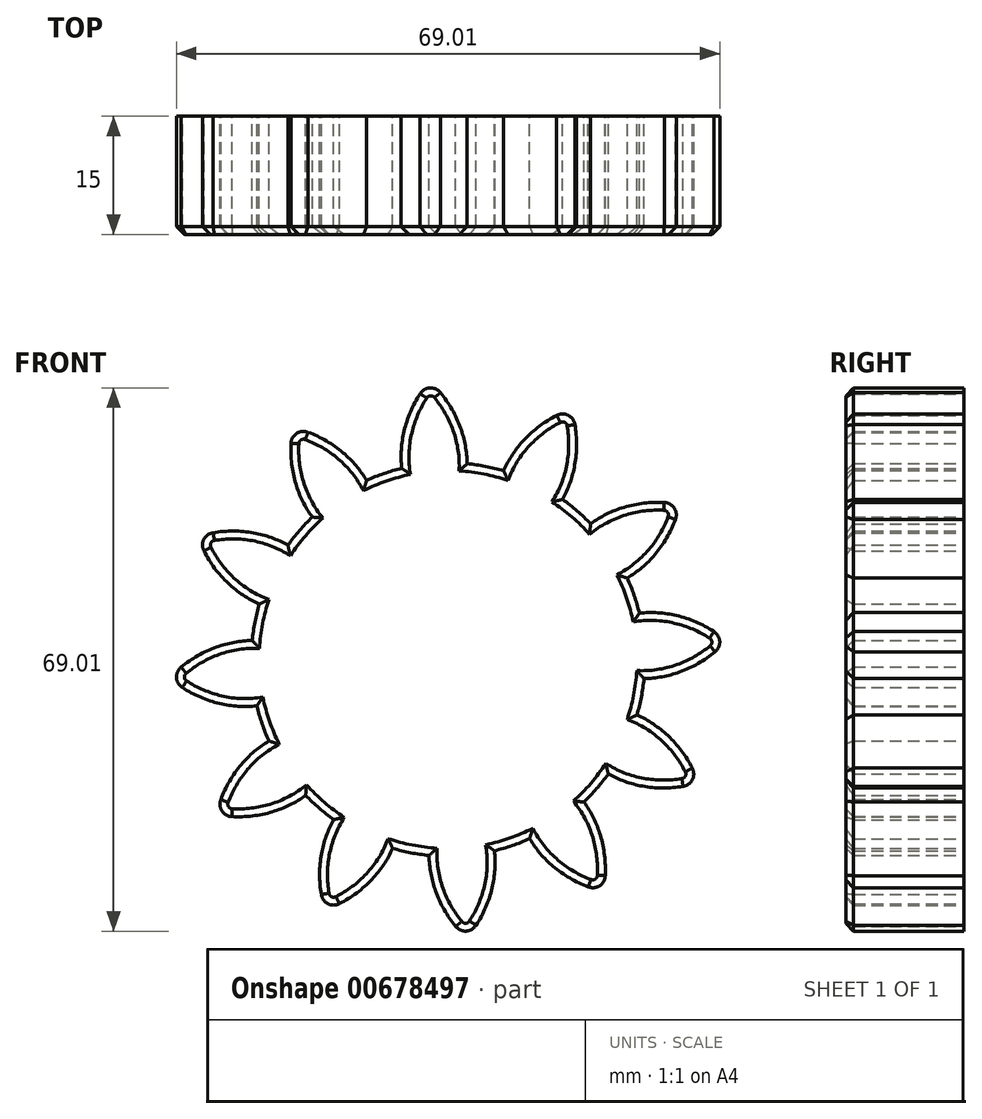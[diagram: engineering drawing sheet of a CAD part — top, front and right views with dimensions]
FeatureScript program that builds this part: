
annotation { "Feature Type Name" : "Feature", "Feature Type Description" : "" }
export const myFeature = defineFeature(function(context is Context, id is Id, definition is map)
    precondition{}
    {
        {
            var Q0;
            Q0=qCreatedBy(makeId("Front.planeOp"),FACE);
            var sketch = newSketch(context, id + "F0", { "sketchPlane" : qUnion([Q0])});
            skLineSegment(sketch, "E0", {"start": v(0, 27.14) * mm, "end": v(-50.23, 27.14) * mm, "construction": true});
            skArc(sketch, "E1", {"start": v(1.46, 32.31) * mm, "mid": v(0.38, 34.66) * mm, "end": v(-1.1, 36.8) * mm});
            skArc(sketch, "E2", {"start": v(2.3, 27.66) * mm, "mid": v(2.08, 30.02) * mm, "end": v(1.46, 32.31) * mm});
            skArc(sketch, "E3.MirrorCS", {"start": v(-5.7, 31.9) * mm, "mid": v(-4.9, 34.36) * mm, "end": v(-3.68, 36.65) * mm});
            skArc(sketch, "E4.MirrorCS", {"start": v(-6.01, 27.2) * mm, "mid": v(-6.06, 29.56) * mm, "end": v(-5.7, 31.9) * mm});
            skArc(sketch, "E5", {"start": v(-1.1, 36.8) * mm, "mid": v(-2.42, 37.4) * mm, "end": v(-3.68, 36.65) * mm});
            skCircle(sketch, "E6", {"center": v(-0.12, 2.9) * mm, "radius": 25 * mm});
            skPoint(sketch, "E6.third.point", {"position": v(0, -22.1) * mm});
            skSolve(sketch);
        }
        {
            var Q0;
            {var subQ0=sQuery(id+"F0.wireOp",EDGE,"RK60bynm-IzvD-K68g-9gkx-ry8jvZAD5OEx");var subQ1=makeQuery(id+"F0.imprint","INTERSECT",VERTEX,{"derivedFrom":[subQ0,sQuery(id+"F0.wireOp",EDGE,"Z6IcxZwb-bq2U-V9Vx-4kxp-I47h1Pi9oaTY")]});Q0=makeQuery(id+"F0.imprint","IMPRINT",FACE,{"disambiguationData":[TD([[makeQuery(id+"F0.imprint","IMPRINT",EDGE,{"disambiguationData":[TD([[subQ1,-1.0]])],"derivedFrom":subQ0}),1.0]])]});}
            var Q1;
            Q1=makeQuery(id+"F0.imprint","IMPRINT",FACE,{"disambiguationData":[TD([[makeQuery(id+"F0.imprint","IMPRINT",EDGE,{"derivedFrom":sQuery(id+"F0.wireOp",EDGE,"Ryq1vTBh-KGyn-BjgW-E2gL-FmNbt1kOCbOb")}),1.0]])]});
            var Q2;
            {var subQ2=sQuery(id+"F0.wireOp",EDGE,"E1");Q2=makeQuery(id+"F0.imprint","IMPRINT",FACE,{"disambiguationData":[TD([[makeQuery(id+"F0.imprint","IMPRINT",EDGE,{"derivedFrom":subQ2}),1.0]])]});}
            var Q3;
            {var subQ0=sQuery(id+"F0.wireOp",EDGE,"E6");var subQ1=makeQuery(id+"F0.imprint","INTERSECT",VERTEX,{"derivedFrom":[sQuery(id+"F0.wireOp",EDGE,"E2"),subQ0]});Q3=makeQuery(id+"F0.imprint","IMPRINT",FACE,{"disambiguationData":[TD([[makeQuery(id+"F0.imprint","IMPRINT",EDGE,{"disambiguationData":[TD([[subQ1,-1.0]])],"derivedFrom":subQ0}),1.0]])]});}
            extrude(context, id + "F1", {"entities" : qUnion([Q0, Q1, Q2, Q3]), "depth" : 15 * mm, "offsetDistance" : 25 * mm, "flatOperationType" : FlatOperationType.REMOVE, "domain" : OperationDomain.MODEL});
        }
        {
            var Q0;
            Q0=makeQuery(id+"F1.opExtrude","CAP_EDGE",EDGE,{"disambiguationData":[OSD([sQuery(id+"F0.wireOp",EDGE,"RK60bynm-IzvD-K68g-9gkx-ry8jvZAD5OEx")])],"isStart":false});
            var Q1;
            Q1=makeQuery(id+"F1.opExtrude","CAP_EDGE",EDGE,{"disambiguationData":[OSD([sQuery(id+"F0.wireOp",EDGE,"Z6IcxZwb-bq2U-V9Vx-4kxp-I47h1Pi9oaTY")])],"isStart":false});
            var Q2;
            Q2=makeQuery(id+"F1.opExtrude","CAP_EDGE",EDGE,{"disambiguationData":[OSD([sQuery(id+"F0.wireOp",EDGE,"820baf2d-91e2-4098-a2de-25aef56e50b20.MirrorCS")])],"isStart":false});
            var Q3;
            Q3=makeQuery(id+"F1.opExtrude","CAP_EDGE",EDGE,{"disambiguationData":[OSD([sQuery(id+"F0.wireOp",EDGE,"Ryq1vTBh-KGyn-BjgW-E2gL-FmNbt1kOCbOb")])],"isStart":false});
            var Q4;
            Q4=makeQuery(id+"F1.opExtrude","CAP_EDGE",EDGE,{"disambiguationData":[OSD([sQuery(id+"F0.wireOp",EDGE,"af102f90-dcfa-482e-b3ce-9af33d462acd0.MirrorCS")])],"isStart":false});
            var Q5;
            Q5=makeQuery(id+"F1.opExtrude","CAP_EDGE",EDGE,{"disambiguationData":[OSD([sQuery(id+"F0.wireOp",EDGE,"u4poM2OA-MWgP-n9JE-3Qco-4fi2lhRNjPUH")])],"isStart":false});
            var Q6;
            Q6=makeQuery(id+"F1.opExtrude","CAP_EDGE",EDGE,{"disambiguationData":[OSD([sQuery(id+"F0.wireOp",EDGE,"E4.MirrorCS")])],"isStart":false});
            var Q7;
            Q7=makeQuery(id+"F1.opExtrude","CAP_EDGE",EDGE,{"disambiguationData":[OSD([sQuery(id+"F0.wireOp",EDGE,"E2")])],"isStart":false});
            var Q8;
            Q8=makeQuery(id+"F1.opExtrude","CAP_EDGE",EDGE,{"disambiguationData":[OSD([sQuery(id+"F0.wireOp",EDGE,"E5")])],"isStart":false});
            var Q9;
            Q9=makeQuery(id+"F1.opExtrude","CAP_EDGE",EDGE,{"disambiguationData":[OSD([sQuery(id+"F0.wireOp",EDGE,"E6")])],"isStart":false});
            chamfer(context, id + "F2", {"entities" : qUnion([Q0, Q1, Q2, Q3, Q4, Q5, Q6, Q7, Q8, Q9]), "width" : 1 * mm, "tangentPropagation" : true});
        }
        {
            var Q0;
            Q0=makeQuery(id+"F1.opExtrude","SWEPT_BODY",BODY,{"disambiguationData":[OSD([sQuery(id+"F0.wireOp",EDGE,"RK60bynm-IzvD-K68g-9gkx-ry8jvZAD5OEx"),sQuery(id+"F0.wireOp",EDGE,"E1"),sQuery(id+"F0.wireOp",EDGE,"E2"),sQuery(id+"F0.wireOp",EDGE,"E3.MirrorCS"),sQuery(id+"F0.wireOp",EDGE,"E4.MirrorCS"),sQuery(id+"F0.wireOp",EDGE,"E5")])]});
            var Q1;
            Q1=makeQuery(id+"F1.opExtrude","SWEPT_FACE",FACE,{"disambiguationData":[OSD([sQuery(id+"F0.wireOp",EDGE,"E6")])]});
            circularPattern(context, id + "F3", {"operationType" : NewBodyOperationType.ADD, "entities" : qUnion([Q0]), "axis" : qUnion([Q1]), "angle" : 360 * degree, "instanceCount" : 12, "equalSpace" : true});
        }
    });
